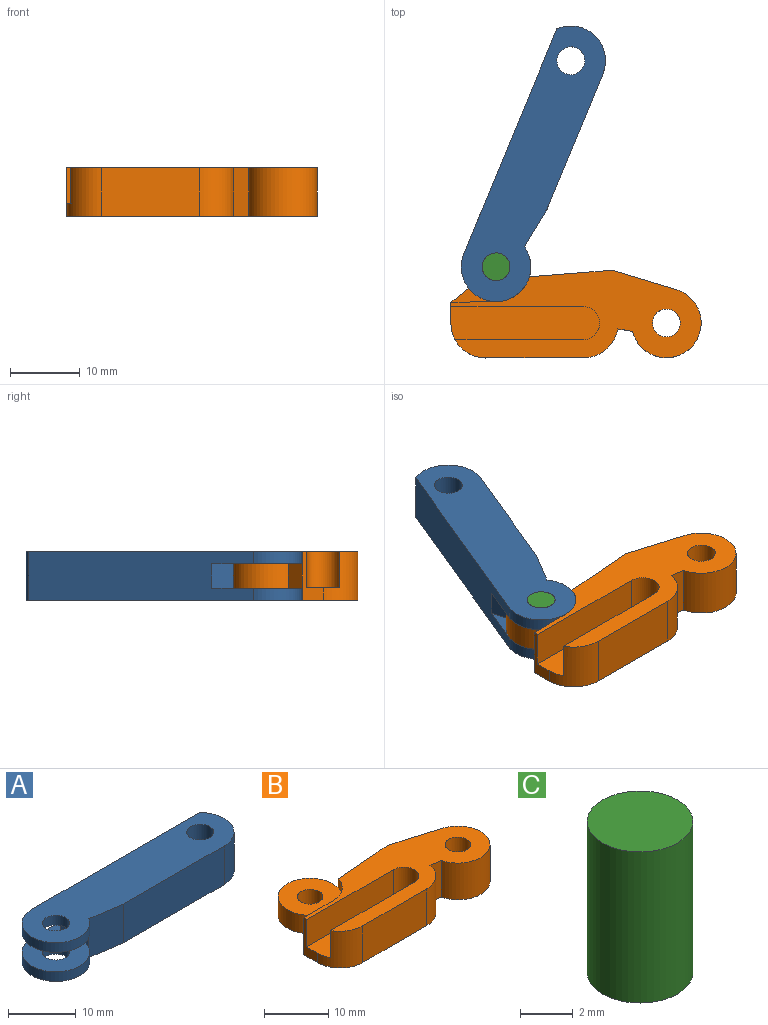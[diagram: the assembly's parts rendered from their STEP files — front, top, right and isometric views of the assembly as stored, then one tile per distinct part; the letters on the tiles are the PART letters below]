
ASSEMBLY  parts=3 mates=2
PART A: 15 faces, bbox 41.5x10x7 mm
  f0: plane 34.97x7mm, normal (0,1,0), area 222mm2, adj f1,f4,f7,f8,f10,f11,f12,f13
  f1: cylinder r=5mm len=10mm, axis (0,0,-1), area 36.3mm2, adj f0,f6,f8,f11
  f2: cylinder r=2mm len=4mm, axis (0,0,-1), area 22mm2, adj f8,f11
  f3: plane 21x7mm, normal (0,-1,0), area 147mm2, adj f4,f6,f7,f8
  f4: cylinder r=5mm len=8.6mm, axis (0,0,-1), area 83.1mm2, adj f0,f3,f7,f8
  f5: cylinder r=2mm len=7mm, axis (0,0,-1), area 88mm2, adj f7,f8
  f6: plane 7x6.27mm, normal (-0.15,-0.99,0), area 44.4mm2, adj f1,f3,f7,f8,f9,f12
  f7: plane 41.5x10mm, normal (0,0,1), area 321mm2, adj f0,f3,f4,f5,f6,f12,f14
  f8: plane 41.5x10mm, normal (0,0,-1), area 321mm2, adj f0,f1,f2,f3,f4,f5,f6
  f9: cylinder r=5mm len=5.71mm, axis (0,0,1), area 21.3mm2, adj f6,f10,f11,f13
  f10: plane 3.5x2.54mm, normal (-0.61,0.79,0), area 11.2mm2, adj f0,f9,f11,f13
  f11: plane 11.5x10mm, normal (0,0,1), area 70.8mm2, adj f0,f1,f2,f9,f10
  f12: cylinder r=5mm len=10mm, axis (0,0,1), area 36.3mm2, adj f0,f6,f7,f13
  f13: plane 11.5x10mm, normal (0,0,-1), area 70.8mm2, adj f0,f9,f10,f12,f14
  f14: cylinder r=2mm len=4mm, axis (0,0,1), area 22mm2, adj f7,f13
PART B: 24 faces, bbox 36x18.1x7 mm
  f0: plane 5.25x2.57mm, normal (-0.62,0.79,0), area 11.4mm2, adj f1,f3,f4,f19,f20,f23
  f1: cylinder r=5mm len=10mm, axis (0,0,-1), area 71.7mm2, adj f0,f11,f20,f23
  f2: cylinder r=2mm len=4mm, axis (0,0,-1), area 44mm2, adj f20,f23
  f3: plane 36x12.61mm, normal (0,0,-1), area 332.2mm2, adj f0,f4,f5,f7,f8,f9,f10,f11
  f4: plane 7x3mm, normal (-1,0,0), area 8.8mm2, adj f0,f3,f5,f6,f14,f17,f21
  f5: cylinder r=5mm len=7mm, axis (0,0,-1), area 42.3mm2, adj f3,f4,f6,f13,f15,f17
  f6: plane 36x12.61mm, normal (0,0,1), area 234.3mm2, adj f4,f5,f7,f8,f9,f10,f11,f12
  f7: cylinder r=5mm len=7mm, axis (0,0,-1), area 49.1mm2, adj f3,f6,f8,f13
  f8: plane 7x2.15mm, normal (-0.17,-0.99,0), area 15.3mm2, adj f3,f6,f7,f9
  f9: cylinder r=5mm len=9.85mm, axis (0,0,-1), area 146.1mm2, adj f3,f6,f8,f10
  f10: plane 9.25x7mm, normal (0.29,0.96,0), area 67.7mm2, adj f3,f6,f9,f11
  f11: plane 11.91x7mm, normal (-0.08,1,0), area 83.6mm2, adj f1,f3,f6,f10,f18,f22
  f12: cylinder r=2mm len=7mm, axis (0,0,-1), area 88mm2, adj f3,f6
  f13: plane 14.07x7mm, normal (0,-1,0), area 98.5mm2, adj f3,f5,f6,f7
  f14: plane 19.08x5.2mm, normal (0,-1,0), area 99.2mm2, adj f4,f6,f16,f17
  f15: plane 18.49x5.2mm, normal (0,1,0), area 96.1mm2, adj f5,f6,f16,f17
  f16: cylinder r=2.35mm len=5.2mm, axis (0,0,1), area 38.4mm2, adj f6,f14,f15,f17
  f17: plane 21.43x4.7mm, normal (0,0,1), area 97.9mm2, adj f4,f5,f14,f15,f16
  f18: cylinder r=5mm len=4.72mm, axis (0,0,-1), area 11.1mm2, adj f3,f11,f19,f20
  f19: plane 6.57x1.75mm, normal (-0.01,1,0), area 11.5mm2, adj f0,f3,f18,f20
  f20: plane 11.49x10.1mm, normal (0,0,-1), area 70.9mm2, adj f0,f1,f2,f18,f19
  f21: plane 6.58x1.75mm, normal (-0.02,1,0), area 11.5mm2, adj f4,f6,f22,f23
  f22: cylinder r=5mm len=4.71mm, axis (0,0,1), area 11.1mm2, adj f6,f11,f21,f23
  f23: plane 11.5x10.1mm, normal (0,0,1), area 70.9mm2, adj f0,f1,f2,f21,f22
PART C: 3 faces, bbox 4x4x7 mm
  f0: cylinder r=2mm len=7mm, axis (0,0,-1), area 88mm2, adj f1,f2
  f1: plane 4x4mm, normal (0,0,1), area 12.6mm2, adj f0
  f2: plane 4x4mm, normal (0,0,-1), area 12.6mm2, adj f0
PLACE A rot(axis=(0,0,1),67.5deg) t=(8.57,13.61,-4.28)mm
PLACE B t=(8.68,3.27,-4.28)mm fixed
PLACE C t=(15.11,16.36,-4.28)mm
MATE fastened C.f0 <-> B.f1  axis (0,0,1) through (15.11,16.36,2.72)mm
MATE revolute A.f1 <-> C.f0  axis (0,0,1) through (15.11,16.36,2.72)mm
